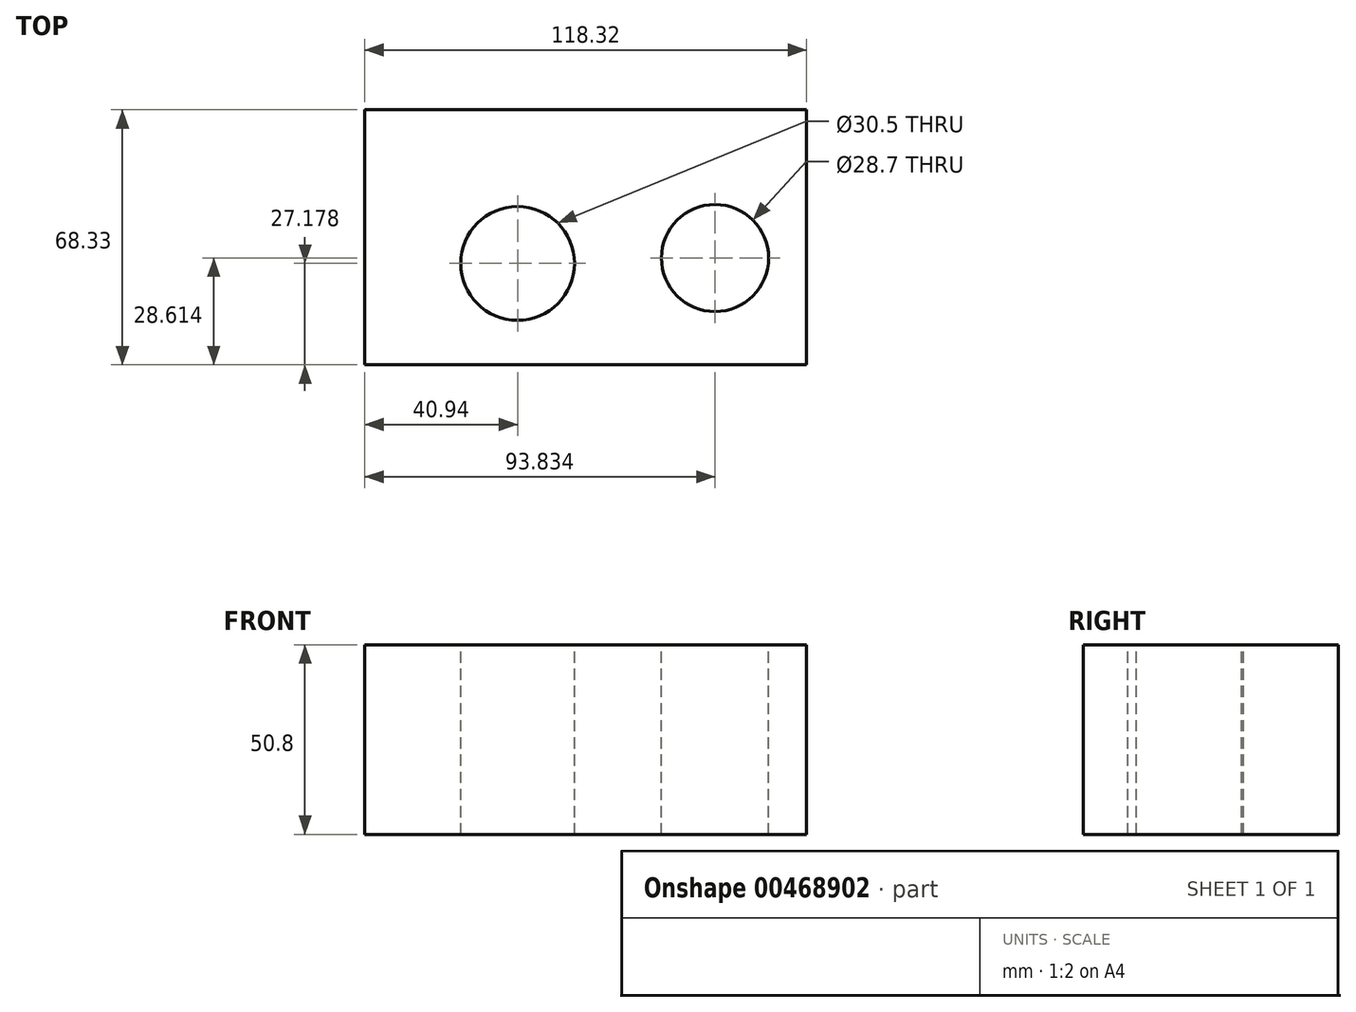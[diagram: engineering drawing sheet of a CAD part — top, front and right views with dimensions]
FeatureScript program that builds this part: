
annotation { "Feature Type Name" : "Feature", "Feature Type Description" : "" }
export const myFeature = defineFeature(function(context is Context, id is Id, definition is map)
    precondition{}
    {
        {
            var Q0;
            Q0=qCreatedBy(makeId("Top.planeOp"),FACE);
            var sketch = newSketch(context, id + "F0", { "sketchPlane" : qUnion([Q0])});
            skLineSegment(sketch, "E0.bottom", {"start": v(-40.94, -34.19) * mm, "end": v(77.38, -34.19) * mm});
            skLineSegment(sketch, "E0.top", {"start": v(-40.94, 34.14) * mm, "end": v(77.38, 34.14) * mm});
            skLineSegment(sketch, "E0.left", {"start": v(-40.94, -34.19) * mm, "end": v(-40.94, 34.14) * mm});
            skLineSegment(sketch, "E0.right", {"start": v(77.38, -34.19) * mm, "end": v(77.38, 34.14) * mm});
            skCircle(sketch, "E1", {"center": v(0, -7.01) * mm, "radius": 15.25 * mm});
            skCircle(sketch, "E2", {"center": v(52.9, -5.58) * mm, "radius": 14.35 * mm});
            skSolve(sketch);
        }
        {
            var Q0;
            Q0=makeQuery(id+"F0.imprint","IMPRINT",FACE,{"disambiguationData":[TD([[makeQuery(id+"F0.imprint","IMPRINT",EDGE,{"derivedFrom":sQuery(id+"F0.wireOp",EDGE,"E0.bottom")}),1.0]])]});
            extrude(context, id + "F1", {"entities" : qUnion([Q0]), "oppositeDirection" : true, "depth" : 50.8 * mm, "offsetDistance" : 25.4 * mm});
        }
    });
